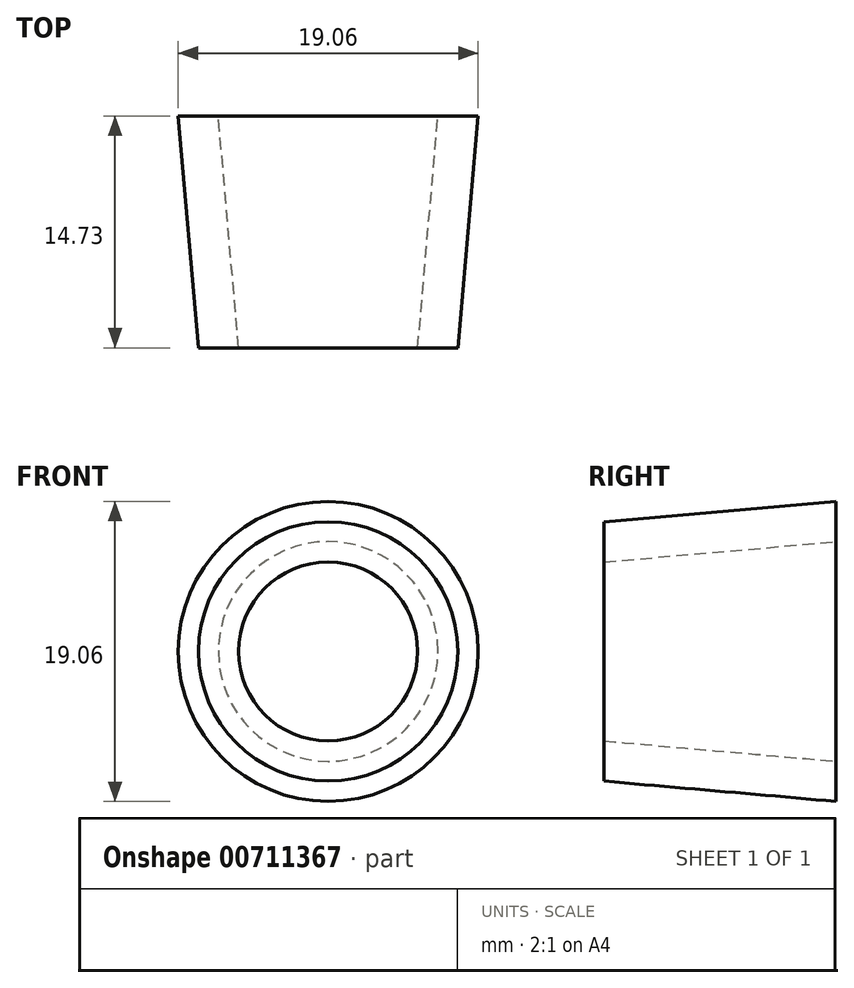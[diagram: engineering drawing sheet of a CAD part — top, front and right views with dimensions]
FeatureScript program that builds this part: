
annotation { "Feature Type Name" : "Feature", "Feature Type Description" : "" }
export const myFeature = defineFeature(function(context is Context, id is Id, definition is map)
    precondition{}
    {
        {
            var Q0;
            Q0=qCreatedBy(makeId("Front.planeOp"),FACE);
            var sketch = newSketch(context, id + "F0", { "sketchPlane" : qUnion([Q0])});
            skCircle(sketch, "E0", {"center": v(0, 0) * mm, "radius": 9.53 * mm});
            skSolve(sketch);
        }
        {
            var Q0;
            Q0=makeQuery(id+"F0.imprint","IMPRINT",FACE,{"disambiguationData":[TD([[makeQuery(id+"F0.imprint","IMPRINT",EDGE,{"derivedFrom":sQuery(id+"F0.wireOp",EDGE,"E0")}),1.0]])]});
            extrude(context, id + "F1", {"entities" : qUnion([Q0]), "depth" : 14.73 * mm, "offsetDistance" : 25.4 * mm, "hasDraft" : true, "draftAngle" : 5 * degree, "draftPullDirection" : true});
        }
        {
            var Q0;
            Q0=makeQuery(id+"F1.opExtrude","CAP_FACE",FACE,{"disambiguationData":[OSD([sQuery(id+"F0.wireOp",EDGE,"E0")])],"isStart":false});
            var Q1;
            Q1=makeQuery(id+"F1.opExtrude","CAP_FACE",FACE,{"disambiguationData":[OSD([sQuery(id+"F0.wireOp",EDGE,"E0")])],"isStart":true});
            shell(context, id + "F2", {"entities" : qUnion([Q0, Q1]), "thickness" : 2.54 * mm});
        }
    });
